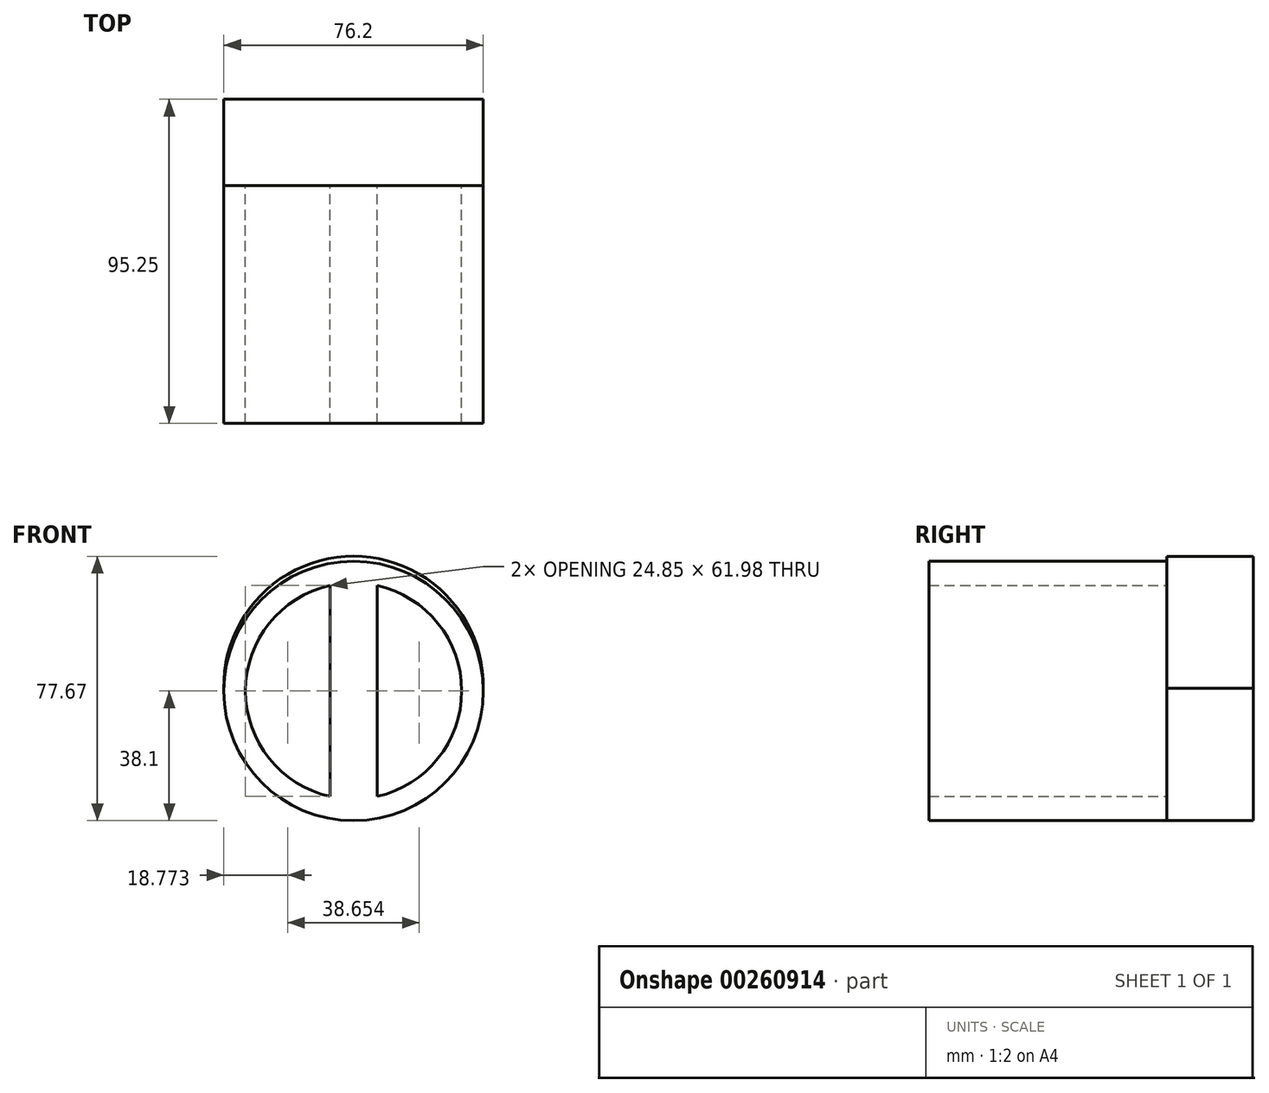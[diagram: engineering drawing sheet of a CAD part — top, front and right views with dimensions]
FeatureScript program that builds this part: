
annotation { "Feature Type Name" : "Feature", "Feature Type Description" : "" }
export const myFeature = defineFeature(function(context is Context, id is Id, definition is map)
    precondition{}
    {
        {
            var Q0;
            Q0=qCreatedBy(makeId("Front.planeOp"),FACE);
            var sketch = newSketch(context, id + "F0", { "sketchPlane" : qUnion([Q0])});
            skCircle(sketch, "E0", {"center": v(0, 0) * mm, "radius": 38.1 * mm});
            skCircle(sketch, "E1", {"center": v(0, 0) * mm, "radius": 31.75 * mm});
            skLineSegment(sketch, "E2", {"start": v(6.9, 31) * mm, "end": v(6.9, -31) * mm});
            skLineSegment(sketch, "E3", {"start": v(-6.9, 31) * mm, "end": v(-6.9, -31) * mm});
            skCircle(sketch, "E4", {"center": v(0, 1.47) * mm, "radius": 38.1 * mm});
            skSolve(sketch);
        }
        {
            var Q0;
            Q0=makeQuery(id+"F0.imprint","IMPRINT",FACE,{"disambiguationData":[TD([[makeQuery(id+"F0.imprint","IMPRINT",EDGE,{"derivedFrom":sQuery(id+"F0.wireOp",EDGE,"E0")}),1.0]])]});
            var Q1;
            {var subQ0=sQuery(id+"F0.wireOp",EDGE,"E2");Q1=makeQuery(id+"F0.imprint","IMPRINT",FACE,{"disambiguationData":[TD([[makeQuery(id+"F0.imprint","IMPRINT",EDGE,{"derivedFrom":subQ0}),-1.0]])]});}
            var Q2;
            {var subQ7=sQuery(id+"F0.wireOp",EDGE,"E4");var subQ8=sQuery(id+"F0.wireOp",EDGE,"E0");var subQ9=makeQuery(id+"F0.imprint","INTERSECT",VERTEX,{"disambiguationData":[OD(0.0)],"derivedFrom":[subQ8,subQ7]});Q2=makeQuery(id+"F0.imprint","IMPRINT",FACE,{"disambiguationData":[TD([[makeQuery(id+"F0.imprint","IMPRINT",EDGE,{"disambiguationData":[TD([[subQ9,1.0]])],"derivedFrom":subQ8}),1.0]])]});}
            extrude(context, id + "F1", {"entities" : qUnion([Q0, Q1, Q2]), "depth" : 69.85 * mm});
        }
        {
            var Q0;
            Q0 = qSketchRegion(id + "F0", true);
            var Q1;
            {var subQ0=sQuery(id+"F0.wireOp",EDGE,"E3");Q1=makeQuery(id+"F0.imprint","IMPRINT",FACE,{"disambiguationData":[TD([[makeQuery(id+"F0.imprint","IMPRINT",EDGE,{"derivedFrom":subQ0}),-1.0]])]});}
            var Q2;
            {var subQ0=sQuery(id+"F0.wireOp",EDGE,"E2");Q2=makeQuery(id+"F0.imprint","IMPRINT",FACE,{"disambiguationData":[TD([[makeQuery(id+"F0.imprint","IMPRINT",EDGE,{"derivedFrom":subQ0}),1.0]])]});}
            var Q3;
            {var subQ0=sQuery(id+"F0.wireOp",EDGE,"E2");Q3=makeQuery(id+"F0.imprint","IMPRINT",FACE,{"disambiguationData":[TD([[makeQuery(id+"F0.imprint","IMPRINT",EDGE,{"derivedFrom":subQ0}),-1.0]])]});}
            extrude(context, id + "F2", {"entities" : qUnion([Q0, Q1, Q2, Q3]), "oppositeDirection" : true, "depth" : 25.4 * mm});
        }
    });
